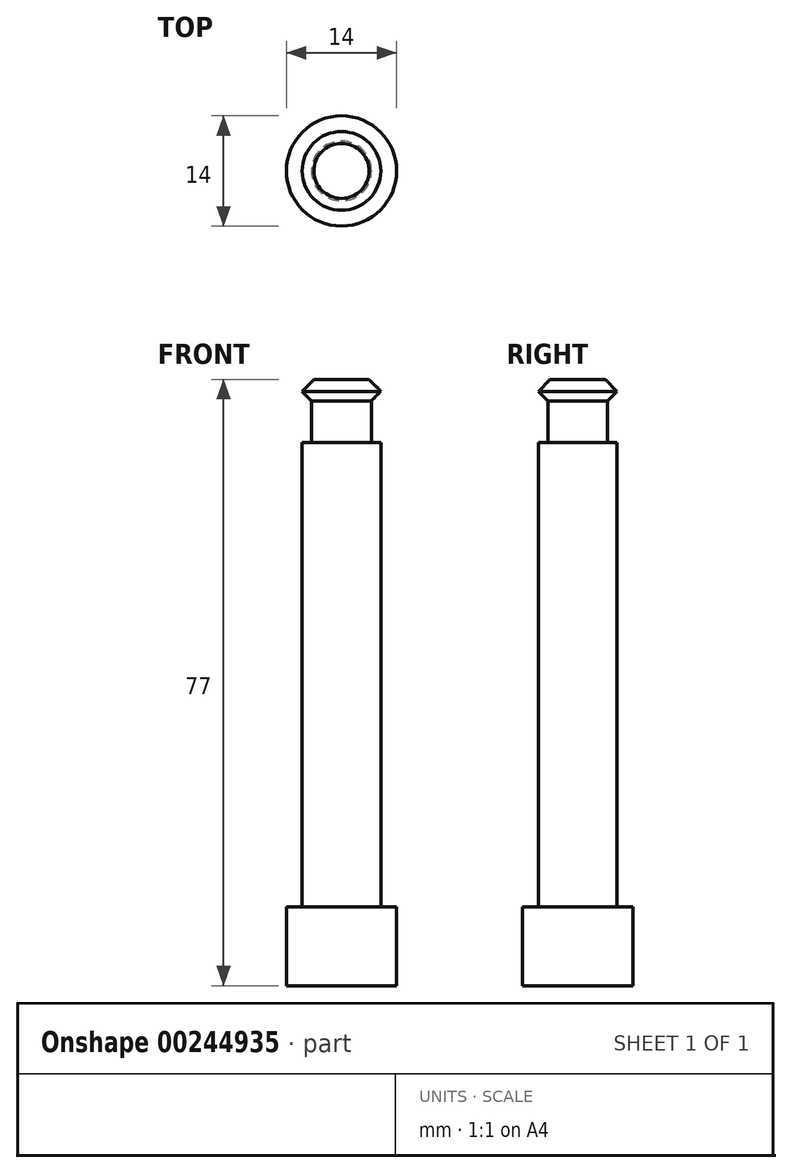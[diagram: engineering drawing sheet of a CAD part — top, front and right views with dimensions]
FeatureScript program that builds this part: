
annotation { "Feature Type Name" : "Feature", "Feature Type Description" : "" }
export const myFeature = defineFeature(function(context is Context, id is Id, definition is map)
    precondition{}
    {
        {
            var Q0;
            Q0=qCreatedBy(makeId("Top.planeOp"),FACE);
            var sketch = newSketch(context, id + "F0", { "sketchPlane" : qUnion([Q0])});
            skCircle(sketch, "E0", {"center": v(0, 0) * mm, "radius": 5 * mm});
            skSolve(sketch);
        }
        {
            var Q0;
            Q0 = qSketchRegion(id + "F0", true);
            extrude(context, id + "F1", {"entities" : qUnion([Q0]), "depth" : 77 * mm});
        }
        {
            var Q0;
            Q0=qCreatedBy(makeId("Front.planeOp"),FACE);
            var sketch = newSketch(context, id + "F2", { "sketchPlane" : qUnion([Q0])});
            skLineSegment(sketch, "E1", {"start": v(0, 0) * mm, "end": v(0, 69) * mm});
            skLineSegment(sketch, "E2", {"start": v(0, 69) * mm, "end": v(3.8, 69) * mm});
            skLineSegment(sketch, "E3.bottom", {"start": v(3.8, 69) * mm, "end": v(6.2, 69) * mm});
            skLineSegment(sketch, "E3.top", {"start": v(3.8, 74) * mm, "end": v(6.2, 74) * mm});
            skLineSegment(sketch, "E3.left", {"start": v(3.8, 69) * mm, "end": v(3.8, 74) * mm});
            skLineSegment(sketch, "E3.right", {"start": v(6.2, 69) * mm, "end": v(6.2, 74) * mm});
            skSolve(sketch);
        }
        {
            var Q0;
            Q0=qCreatedBy(makeId("Top.planeOp"),FACE);
            var sketch = newSketch(context, id + "F3", { "sketchPlane" : qUnion([Q0])});
            skCircle(sketch, "E4", {"center": v(0, 0) * mm, "radius": 7 * mm});
            skSolve(sketch);
        }
        {
            var Q0;
            Q0 = qSketchRegion(id + "F3", true);
            extrude(context, id + "F4", {"entities" : qUnion([Q0]), "operationType" : NewBodyOperationType.ADD, "depth" : 10 * mm});
        }
        {
            var Q0;
            Q0 = qSketchRegion(id + "F2", true);
            var Q1;
            Q1=makeQuery(id+"F1.opExtrude","CAP_EDGE",EDGE,{"disambiguationData":[OSD([sQuery(id+"F0.wireOp",EDGE,"E0")])],"isStart":false});
            sweep(context, id + "F5", {"operationType" : NewBodyOperationType.REMOVE, "profiles" : qUnion([Q0]), "path" : qUnion([Q1])});
        }
        {
            var Q0;
            Q0=makeQuery(id+"F1.opExtrude","CAP_EDGE",EDGE,{"disambiguationData":[OSD([sQuery(id+"F0.wireOp",EDGE,"E0")])],"isStart":false});
            var Q1;
            {var subQ0=sQuery(id+"F0.wireOp",EDGE,"E0");Q1=makeQuery(id+"F5.boolean.opBoolean","INTERSECT",EDGE,{"derivedFrom":[makeQuery(id+"F1.opExtrude","SWEPT_FACE",FACE,{"disambiguationData":[OSD([subQ0])]}),makeQuery(id+"F5.opSweep","SWEPT_FACE",FACE,{"disambiguationData":[OSD([subQ0,sQuery(id+"F2.wireOp",EDGE,"E3.top")])]})]});}
            chamfer(context, id + "F6", {"entities" : qUnion([Q0, Q1]), "width" : 1.5 * mm, "tangentPropagation" : true});
        }
    });
